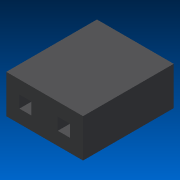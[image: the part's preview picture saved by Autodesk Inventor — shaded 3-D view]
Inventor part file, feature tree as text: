
AUTODESK INVENTOR PART (.ipt)
format: ipt  version: 2015 SP1 (Build 190203100, 203)  size: 88,576 bytes
history: native  units: mm
features: extrude x2, sketch x2, other x1
ambient origin geometry x8: Origin, YZ Plane, XZ Plane, XY Plane, X Axis, Y Axis, Z Axis, Center Point
bodies: Body1 (feature_tree)
feature tree (5):
  other  "Твердое тело1"
  extrude  "Выдавливание1"  Depth=5.08mm
  extrude  "Выдавливание2"  Depth=2.54mm
  sketch  "Эскиз1"
  sketch  "Эскиз2"
